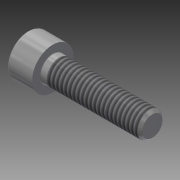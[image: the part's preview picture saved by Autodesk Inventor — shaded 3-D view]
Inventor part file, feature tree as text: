
AUTODESK INVENTOR PART (.ipt)
format: ipt  version: 2018 (Build 220112000, 112)  size: 193,536 bytes
history: native  units: mm (DEFAULTED — no unit token found)
features: sketch x2, extrude x1, plane x1, fillet x1
ambient origin geometry x7: Origin, YZ Plane, XY Plane, X Axis, Y Axis, Z Axis, Center Point
bodies: Solid1 (feature_tree), Body (feature_tree)
feature tree (5):
  extrude  "Slot"  Depth=4.826mm
  plane  "Work Plane1"
  fillet  "Fillet2"  Radius=4.826mm
  sketch  "Sketch1"  dims[d1=17.859048mm d2=1.190852mm d3=4.826mm]
  sketch  "Sketch2"  dims[d4=2.286mm d5=60.0deg d6=4.826mm d7=4.826mm d8=4.575385mm d9=7.9248mm d10=90.0deg d11=10.0mm d12=0.0mm d13=17.859048mm d14=0.0mm d15=0.47244mm d16=0.47244mm d17=0.4572mm d19=0.0mm d26=19.05mm d27=45.0deg d28=0.0mm d29=0.0mm d30=0.1524mm]
